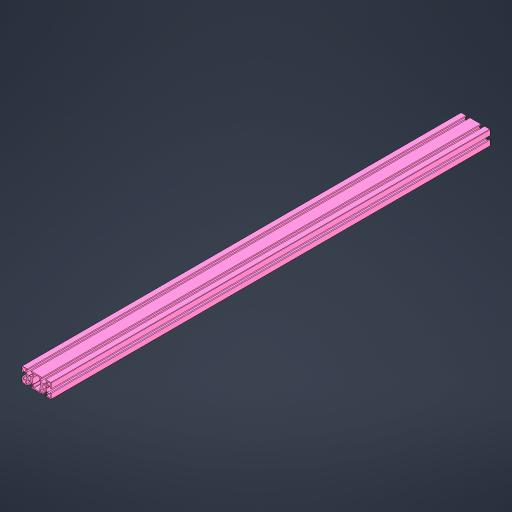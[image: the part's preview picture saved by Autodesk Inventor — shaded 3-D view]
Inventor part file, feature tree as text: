
AUTODESK INVENTOR PART (.ipt)
format: ipt  version: 2024 (Build 280153000, 153)  size: 343,040 bytes
history: native  units: mm
features: other x2, extrude x1, sketch x1
ambient origin geometry x8: Origin, YZ Plane, XZ Plane, XY Plane, X Axis, Y Axis, Z Axis, Center Point
bodies: Body1 (feature_tree)
feature tree (4):
  other  "솔리드1"
  extrude  "돌출1"  Depth=40.0mm
  sketch  "스케치1"
  other  "Finish1"
